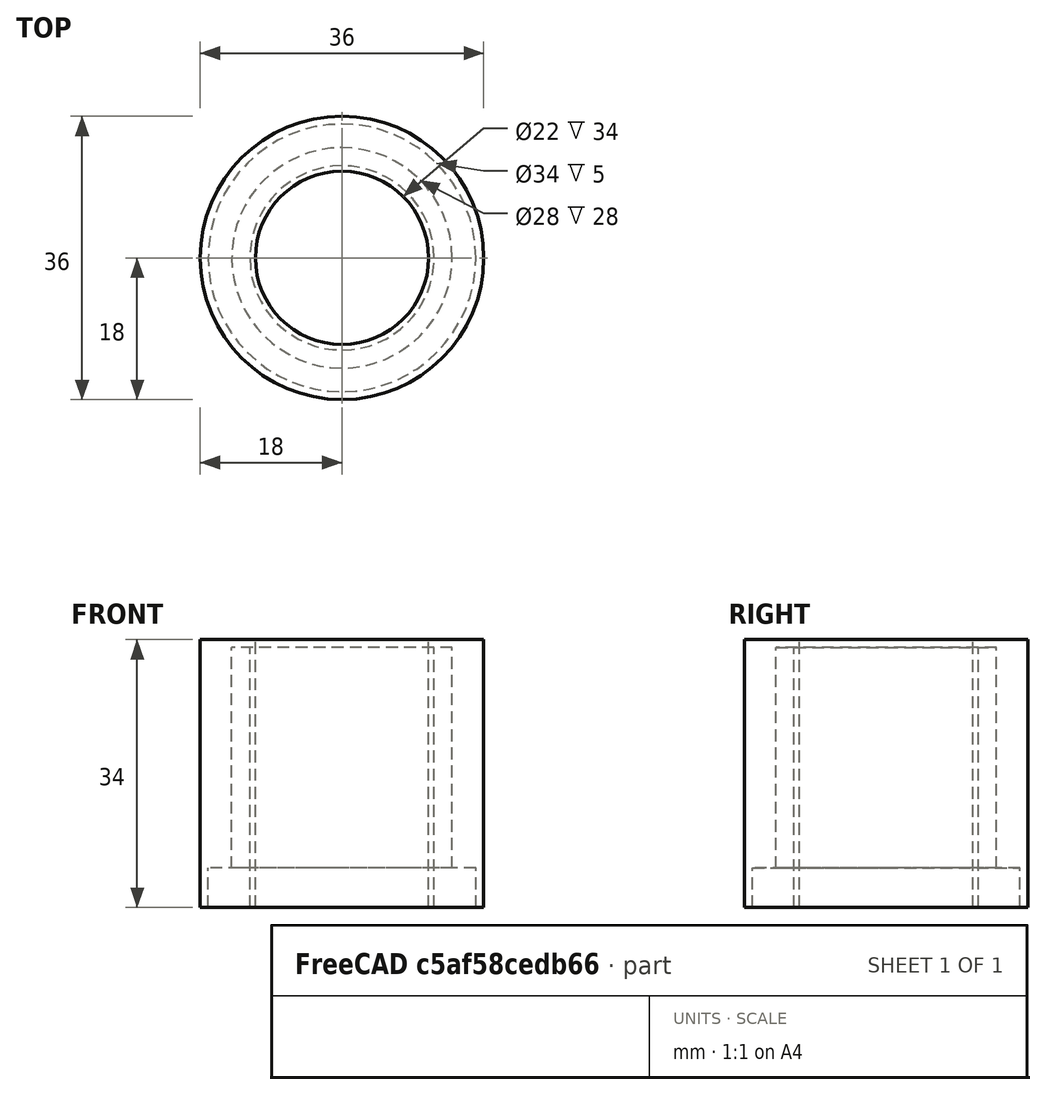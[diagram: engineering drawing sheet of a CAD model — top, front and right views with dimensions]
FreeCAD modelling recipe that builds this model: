
FCSTD DOCUMENT  (FreeCAD 0.17R13509 (Git))
Label: FTInsulator1_negative
License: All rights reserved
LicenseURL: http://en.wikipedia.org/wiki/All_rights_reserved
objects: Part::Cylinder×7, Part::MultiFuse×3, Part::Cut×2, Part::Box×1
note: 13 computed .brp shape members not serialized (recipe doc carries the construction recipe); baked Part::Feature solids carry a one-line shape summary decoded from their .brp

FEATURE [Part::Cylinder] Cylinder084  label="Feedthrough005"
  Angle = 360
  AttacherType = Attacher::AttachEngine3D
  Height = 5
  Placement = pos=(73.66,148,-10) rot=(0,0,1;0rad)
  Radius = 17
  expr: Radius = 17
  expr: Placement.Base.x = 210.81999999999999 / 2 - 31.75
FEATURE [Part::Cylinder] Cylinder088  label="Feedthrough008"
  Angle = 360
  AttacherType = Attacher::AttachEngine3D
  Height = 33
  Placement = pos=(73.66,148,-10) rot=(0,0,1;0rad)
  Radius = 14
  expr: Radius = 28 / 2
  expr: Placement.Base.x = 210.81999999999999 / 2 - 31.75
FEATURE [Part::Cylinder] Cylinder090  label="FTInsInnerHole"
  Angle = 360
  AttacherType = Attacher::AttachEngine3D
  Height = 33
  Placement = pos=(73.66,148,-10) rot=(0,0,1;0rad)
  Radius = 11.7
  expr: Placement.Base.x = 210.81999999999999 / 2 - 31.75
FEATURE [Part::Box] Box016  label="FTInsLug"
  AttacherType = Attacher::AttachEngine3D
  Height = 1
  Length = 1
  Placement = pos=(63,136,-8) rot=(0,0,1;0rad)
  Width = 1
FEATURE [Part::Cylinder] Cylinder093  label="FTInsMount1"
  Angle = 360
  AttacherType = Attacher::AttachEngine3D
  Height = 14
  Placement = pos=(53.66,148,-15) rot=(0,0,1;0rad)
  Radius = 1.5
  expr: Placement.Base.x = 73.659999999999997 - 20
FEATURE [Part::Cylinder] Cylinder094  label="FTInsMount2"
  Angle = 360
  AttacherType = Attacher::AttachEngine3D
  Height = 14
  Placement = pos=(93.66,148,-14) rot=(0,0,1;0rad)
  Radius = 1.5
  expr: Placement.Base.x = 73.659999999999997 + 20
FEATURE [Part::MultiFuse] Fusion038
  Shapes = -> [Cylinder084,Cylinder088,Box016]
FEATURE [Part::MultiFuse] Fusion039
  Shapes = -> [Cylinder094,Cylinder093,Cylinder090]
FEATURE [Part::Cut] Cut010  label="FTInsulator1"
  Base = -> Fusion038
  Placement = pos=(-73.66,-148,-23) rot=(0,0,1;0rad)
  Tool = -> Fusion039
  expr: Placement.Base.z = -33 + 10
FEATURE [Part::Cylinder] Cylinder
  Angle = 360
  AttacherType = Attacher::AttachEngine3D
  Height = 34
  Placement = pos=(0,0,-33) rot=(0,0,1;0rad)
  Radius = 18
FEATURE [Part::Cylinder] Cylinder095
  Angle = 360
  AttacherType = Attacher::AttachEngine3D
  Height = 34
  Placement = pos=(0,0,-33) rot=(0,0,1;0rad)
  Radius = 11
FEATURE [Part::MultiFuse] Fusion
  Shapes = -> [Cylinder095,Cut010]
FEATURE [Part::Cut] Cut
  Base = -> Cylinder
  Tool = -> Fusion
